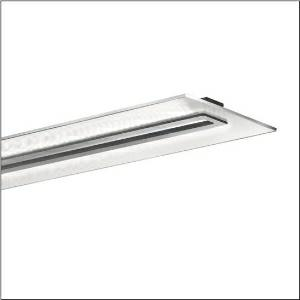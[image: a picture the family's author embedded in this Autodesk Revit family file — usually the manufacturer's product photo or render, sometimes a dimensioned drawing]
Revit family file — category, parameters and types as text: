
# Revit family: vega_r__11_5mn238dlc0s_c747
name_source: partatom
category: Lighting Fixtures
units: mm (PartAtom-declared; Revit-internal decimal feet)

## family parameters
Cut with Voids When Loaded = No
Host = Face
Light Source = No
Part Type = Normal
Room Calculation Point = No
Round Connector Dimension = Use Diameter
Shared = No

## types (1)
- --- (1 x LED 4000K / CRI = 80 (unbekannt), 4300 lm, 4000K)
    Apparent Load = 31 VA
    CIE Flux Codes = 61 86 97 62 100
    Color Rendering = 80
    Color Temperature = 4000K
    Default Elevation = 1800 mm
    Description = Vega® 11, office luminaire, primary light control with prismatic reflector, of PMMA, transparent prismatic structure, CAT 2 (L<= 1500cd/m²), light emission: direct/indirect distribution, primary light characteristic: symmetric, installation type: suspended mounting, surface-mounted, LED, rated luminous flux: 4.300lm, luminous efficacy: 139lm/W, light colour: 840, colour temperature: 4000K, control gear: DALI, with terminal, 3+2-pole, max. 2.5mm², mains connection: 230V, AC, 50Hz, connection cable inclusive, cable length: 1,5m, rated input power: 31W, luminaire housing, rectangular, rounded, of aluminium section, anodised, metallic grey (RAL 9006), length: 1.250mm, width: 350mm, height: 43mm, luminaire housing, lower part, of aluminium section, anodised, metallic grey (RAL 9006), of PC, grey, protection rating (complete): IP20, insulation class (complete): insulation class I (protective earthing), certification: CE, permissible operating ambient temperature: 0..+35°C, standard: EN 50419, packaging unit: 1 piece
    Height = 40 mm  [stored 0.131234 ft]
    Lamp = 1 x LED 4000K / CRI >= 80 (unbekannt)
    Lamp Light Flux = 4300 lm
    Lamp count = 1
    Length = 1250 mm
    Luminous efficacy = 139 lm/W
    Manufacturer = Siteco
    ModVariant = No
    Model = 5MN238DLC0S
    Mounting Place = Ceiling
    Mounting Type = Pendant
    Number of Poles = 1
    OnlyDefault = Yes
    Power Factor = 1
    Product Name = Vega® 11
    Product group = office luminaire | ceiling pendant
    ProductGroupID = 904
    Protection Class = Protection class I
    Protection Degree = IP 20
    RLX_Detail_Level = 1
    RLX_Emergency_Light_Flux = 0 lm
    RLX_Emergency_Type = 0
    RLX_Emergency_Type_DB = No
    RlxData = <blob elided: 63045 chars, md5=365c5616>
    Socket = socket
    Standby Power = 0 W
    System Light Flux = 4300 lm
    System Power = 31 W
    Type Comments = factory setting: luminous flux: 100 % | dim-lin: 254 | 231 mA
    Type Image = l_1004807.jpg
    URL = http://relux.com
    VarID = @adj_204012
    Voltage = 0 V
    Weight = 0.00 kg
    Width = 350 mm

note: [stored X ft] marks values corroborated as IEEE doubles in the binary element streams (Revit-internal decimal feet)

## geometry (parser evidence)
native form markers: Blend x4, Sweep x12
no freeform markers — native parametric forms only
